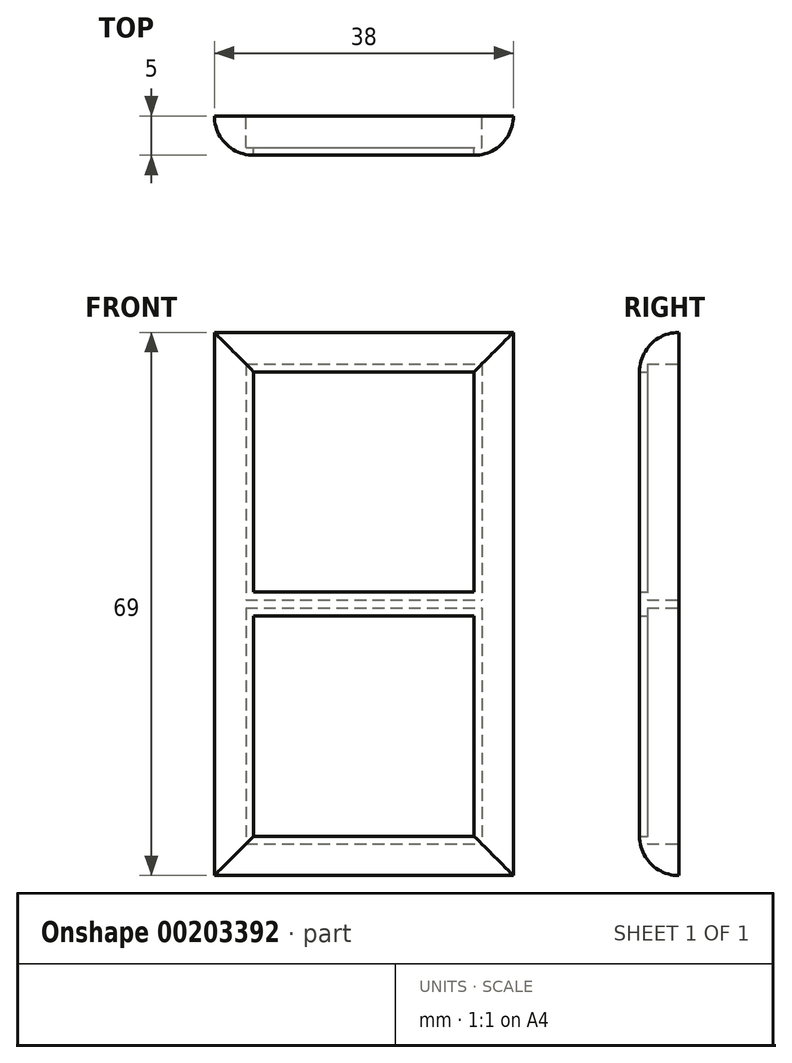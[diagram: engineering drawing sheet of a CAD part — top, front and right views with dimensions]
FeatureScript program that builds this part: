
annotation { "Feature Type Name" : "Feature", "Feature Type Description" : "" }
export const myFeature = defineFeature(function(context is Context, id is Id, definition is map)
    precondition{}
    {
        {
            var Q0;
            Q0=qCreatedBy(makeId("Front.planeOp"),FACE);
            var sketch = newSketch(context, id + "F0", { "sketchPlane" : qUnion([Q0])});
            skLineSegment(sketch, "E0.bottom", {"start": v(-19, 34.5) * mm, "end": v(19, 34.5) * mm});
            skLineSegment(sketch, "E0.top", {"start": v(-19, -34.5) * mm, "end": v(19, -34.5) * mm});
            skLineSegment(sketch, "E0.left", {"start": v(-19, 34.5) * mm, "end": v(-19, -34.5) * mm});
            skLineSegment(sketch, "E0.right", {"start": v(19, 34.5) * mm, "end": v(19, -34.5) * mm});
            skPoint(sketch, "E0.middle", {"position": v(0, 0) * mm});
            skLineSegment(sketch, "E1.bottom", {"start": v(-14, 29.5) * mm, "end": v(14, 29.5) * mm});
            skLineSegment(sketch, "E1.top", {"start": v(-14, -29.5) * mm, "end": v(14, -29.5) * mm});
            skLineSegment(sketch, "E1.left", {"start": v(-14, 29.5) * mm, "end": v(-14, -29.5) * mm});
            skLineSegment(sketch, "E1.right", {"start": v(14, 29.5) * mm, "end": v(14, -29.5) * mm});
            skLineSegment(sketch, "E2.bottom", {"start": v(-15, 30.5) * mm, "end": v(15, 30.5) * mm});
            skLineSegment(sketch, "E2.top", {"start": v(-15, -30.5) * mm, "end": v(15, -30.5) * mm});
            skLineSegment(sketch, "E2.left", {"start": v(-15, 30.5) * mm, "end": v(-15, -30.5) * mm});
            skLineSegment(sketch, "E2.right", {"start": v(15, 30.5) * mm, "end": v(15, -30.5) * mm});
            skLineSegment(sketch, "E3.bottom", {"start": v(-15, 0.5) * mm, "end": v(15, 0.5) * mm});
            skLineSegment(sketch, "E3.top", {"start": v(-15, -0.5) * mm, "end": v(15, -0.5) * mm});
            skLineSegment(sketch, "E3.left", {"start": v(-15, 0.5) * mm, "end": v(-15, -0.5) * mm});
            skLineSegment(sketch, "E3.right", {"start": v(15, 0.5) * mm, "end": v(15, -0.5) * mm});
            skLineSegment(sketch, "E4.bottom", {"start": v(-15, 1.5) * mm, "end": v(15, 1.5) * mm});
            skLineSegment(sketch, "E4.top", {"start": v(-15, -1.5) * mm, "end": v(15, -1.5) * mm});
            skLineSegment(sketch, "E4.left", {"start": v(-15, 1.5) * mm, "end": v(-15, -1.5) * mm});
            skLineSegment(sketch, "E4.right", {"start": v(15, 1.5) * mm, "end": v(15, -1.5) * mm});
            skSolve(sketch);
        }
        {
            var Q0;
            {var subQ7=sQuery(id+"F0.wireOp",EDGE,"E1.top");Q0=makeQuery(id+"F0.imprint","IMPRINT",FACE,{"disambiguationData":[TD([[makeQuery(id+"F0.imprint","IMPRINT",EDGE,{"derivedFrom":subQ7}),-1.0]])]});}
            var Q1;
            {var subQ2=sQuery(id+"F0.wireOp",EDGE,"E1.bottom");Q1=makeQuery(id+"F0.imprint","IMPRINT",FACE,{"disambiguationData":[TD([[makeQuery(id+"F0.imprint","IMPRINT",EDGE,{"derivedFrom":subQ2}),1.0]])]});}
            var Q2;
            {var subQ0=sQuery(id+"F0.wireOp",EDGE,"E1.bottom");Q2=makeQuery(id+"F0.imprint","IMPRINT",FACE,{"disambiguationData":[TD([[makeQuery(id+"F0.imprint","IMPRINT",EDGE,{"derivedFrom":subQ0}),-1.0]])]});}
            var Q3;
            Q3=makeQuery(id+"F0.imprint","IMPRINT",FACE,{"disambiguationData":[TD([[makeQuery(id+"F0.imprint","IMPRINT",EDGE,{"derivedFrom":sQuery(id+"F0.wireOp",EDGE,"E0.bottom")}),-1.0]])]});
            var Q4;
            {var subQ0=sQuery(id+"F0.wireOp",EDGE,"E1.top");Q4=makeQuery(id+"F0.imprint","IMPRINT",FACE,{"disambiguationData":[TD([[makeQuery(id+"F0.imprint","IMPRINT",EDGE,{"derivedFrom":subQ0}),1.0]])]});}
            var Q5;
            {var subQ0=sQuery(id+"F0.wireOp",EDGE,"E4.bottom");var subQ1=sQuery(id+"F0.wireOp",EDGE,"E1.left");var subQ2=makeQuery(id+"F0.imprint","INTERSECT",VERTEX,{"derivedFrom":[subQ1,subQ0]});Q5=makeQuery(id+"F0.imprint","IMPRINT",FACE,{"disambiguationData":[TD([[makeQuery(id+"F0.imprint","IMPRINT",EDGE,{"disambiguationData":[TD([[subQ2,-1.0]])],"derivedFrom":subQ1}),1.0]])]});}
            var Q6;
            {var subQ0=sQuery(id+"F0.wireOp",EDGE,"E3.top");var subQ1=sQuery(id+"F0.wireOp",EDGE,"E1.left");var subQ2=makeQuery(id+"F0.imprint","INTERSECT",VERTEX,{"derivedFrom":[subQ1,subQ0]});Q6=makeQuery(id+"F0.imprint","IMPRINT",FACE,{"disambiguationData":[TD([[makeQuery(id+"F0.imprint","IMPRINT",EDGE,{"disambiguationData":[TD([[subQ2,-1.0]])],"derivedFrom":subQ1}),1.0]])]});}
            var Q7;
            {var subQ0=sQuery(id+"F0.wireOp",EDGE,"E3.bottom");var subQ1=sQuery(id+"F0.wireOp",EDGE,"E1.left");var subQ2=makeQuery(id+"F0.imprint","INTERSECT",VERTEX,{"derivedFrom":[subQ1,subQ0]});Q7=makeQuery(id+"F0.imprint","IMPRINT",FACE,{"disambiguationData":[TD([[makeQuery(id+"F0.imprint","IMPRINT",EDGE,{"disambiguationData":[TD([[subQ2,-1.0]])],"derivedFrom":subQ1}),1.0]])]});}
            var Q8;
            {var subQ0=sQuery(id+"F0.wireOp",EDGE,"E4.bottom");var subQ1=sQuery(id+"F0.wireOp",EDGE,"E1.left");var subQ2=makeQuery(id+"F0.imprint","INTERSECT",VERTEX,{"derivedFrom":[subQ1,subQ0]});Q8=makeQuery(id+"F0.imprint","IMPRINT",FACE,{"disambiguationData":[TD([[makeQuery(id+"F0.imprint","IMPRINT",EDGE,{"disambiguationData":[TD([[subQ2,-1.0]])],"derivedFrom":subQ1}),-1.0]])]});}
            var Q9;
            {var subQ0=sQuery(id+"F0.wireOp",EDGE,"E3.bottom");var subQ1=sQuery(id+"F0.wireOp",EDGE,"E1.left");var subQ2=makeQuery(id+"F0.imprint","INTERSECT",VERTEX,{"derivedFrom":[subQ1,subQ0]});Q9=makeQuery(id+"F0.imprint","IMPRINT",FACE,{"disambiguationData":[TD([[makeQuery(id+"F0.imprint","IMPRINT",EDGE,{"disambiguationData":[TD([[subQ2,-1.0]])],"derivedFrom":subQ1}),-1.0]])]});}
            var Q10;
            {var subQ0=sQuery(id+"F0.wireOp",EDGE,"E3.top");var subQ1=sQuery(id+"F0.wireOp",EDGE,"E1.left");var subQ2=makeQuery(id+"F0.imprint","INTERSECT",VERTEX,{"derivedFrom":[subQ1,subQ0]});Q10=makeQuery(id+"F0.imprint","IMPRINT",FACE,{"disambiguationData":[TD([[makeQuery(id+"F0.imprint","IMPRINT",EDGE,{"disambiguationData":[TD([[subQ2,-1.0]])],"derivedFrom":subQ1}),-1.0]])]});}
            var Q11;
            {var subQ0=sQuery(id+"F0.wireOp",EDGE,"E4.bottom");var subQ1=sQuery(id+"F0.wireOp",EDGE,"E1.right");var subQ2=makeQuery(id+"F0.imprint","INTERSECT",VERTEX,{"derivedFrom":[subQ1,subQ0]});Q11=makeQuery(id+"F0.imprint","IMPRINT",FACE,{"disambiguationData":[TD([[makeQuery(id+"F0.imprint","IMPRINT",EDGE,{"disambiguationData":[TD([[subQ2,-1.0]])],"derivedFrom":subQ1}),1.0]])]});}
            var Q12;
            {var subQ0=sQuery(id+"F0.wireOp",EDGE,"E3.bottom");var subQ1=sQuery(id+"F0.wireOp",EDGE,"E1.right");var subQ2=makeQuery(id+"F0.imprint","INTERSECT",VERTEX,{"derivedFrom":[subQ1,subQ0]});Q12=makeQuery(id+"F0.imprint","IMPRINT",FACE,{"disambiguationData":[TD([[makeQuery(id+"F0.imprint","IMPRINT",EDGE,{"disambiguationData":[TD([[subQ2,-1.0]])],"derivedFrom":subQ1}),1.0]])]});}
            var Q13;
            {var subQ0=sQuery(id+"F0.wireOp",EDGE,"E3.top");var subQ1=sQuery(id+"F0.wireOp",EDGE,"E1.right");var subQ2=makeQuery(id+"F0.imprint","INTERSECT",VERTEX,{"derivedFrom":[subQ1,subQ0]});Q13=makeQuery(id+"F0.imprint","IMPRINT",FACE,{"disambiguationData":[TD([[makeQuery(id+"F0.imprint","IMPRINT",EDGE,{"disambiguationData":[TD([[subQ2,-1.0]])],"derivedFrom":subQ1}),1.0]])]});}
            extrude(context, id + "F1", {"entities" : qUnion([Q0, Q1, Q2, Q3, Q4, Q5, Q6, Q7, Q8, Q9, Q10, Q11, Q12, Q13]), "depth" : 5 * mm});
        }
        {
            var Q0;
            {var subQ0=sQuery(id+"F0.wireOp",EDGE,"E1.bottom");Q0=makeQuery(id+"F0.imprint","IMPRINT",FACE,{"disambiguationData":[TD([[makeQuery(id+"F0.imprint","IMPRINT",EDGE,{"derivedFrom":subQ0}),-1.0]])]});}
            var Q1;
            {var subQ0=sQuery(id+"F0.wireOp",EDGE,"E1.top");Q1=makeQuery(id+"F0.imprint","IMPRINT",FACE,{"disambiguationData":[TD([[makeQuery(id+"F0.imprint","IMPRINT",EDGE,{"derivedFrom":subQ0}),1.0]])]});}
            extrude(context, id + "F2", {"entities" : qUnion([Q0, Q1]), "operationType" : NewBodyOperationType.REMOVE, "depth" : 25 * mm});
        }
        {
            var Q0;
            {var subQ2=sQuery(id+"F0.wireOp",EDGE,"E1.bottom");Q0=makeQuery(id+"F0.imprint","IMPRINT",FACE,{"disambiguationData":[TD([[makeQuery(id+"F0.imprint","IMPRINT",EDGE,{"derivedFrom":subQ2}),1.0]])]});}
            var Q1;
            {var subQ0=sQuery(id+"F0.wireOp",EDGE,"E4.bottom");var subQ1=sQuery(id+"F0.wireOp",EDGE,"E1.right");var subQ2=makeQuery(id+"F0.imprint","INTERSECT",VERTEX,{"derivedFrom":[subQ1,subQ0]});Q1=makeQuery(id+"F0.imprint","IMPRINT",FACE,{"disambiguationData":[TD([[makeQuery(id+"F0.imprint","IMPRINT",EDGE,{"disambiguationData":[TD([[subQ2,-1.0]])],"derivedFrom":subQ1}),1.0]])]});}
            var Q2;
            {var subQ0=sQuery(id+"F0.wireOp",EDGE,"E4.bottom");var subQ1=sQuery(id+"F0.wireOp",EDGE,"E1.left");var subQ2=makeQuery(id+"F0.imprint","INTERSECT",VERTEX,{"derivedFrom":[subQ1,subQ0]});Q2=makeQuery(id+"F0.imprint","IMPRINT",FACE,{"disambiguationData":[TD([[makeQuery(id+"F0.imprint","IMPRINT",EDGE,{"disambiguationData":[TD([[subQ2,-1.0]])],"derivedFrom":subQ1}),1.0]])]});}
            var Q3;
            {var subQ0=sQuery(id+"F0.wireOp",EDGE,"E4.bottom");var subQ1=sQuery(id+"F0.wireOp",EDGE,"E1.left");var subQ2=makeQuery(id+"F0.imprint","INTERSECT",VERTEX,{"derivedFrom":[subQ1,subQ0]});Q3=makeQuery(id+"F0.imprint","IMPRINT",FACE,{"disambiguationData":[TD([[makeQuery(id+"F0.imprint","IMPRINT",EDGE,{"disambiguationData":[TD([[subQ2,-1.0]])],"derivedFrom":subQ1}),-1.0]])]});}
            var Q4;
            {var subQ7=sQuery(id+"F0.wireOp",EDGE,"E1.top");Q4=makeQuery(id+"F0.imprint","IMPRINT",FACE,{"disambiguationData":[TD([[makeQuery(id+"F0.imprint","IMPRINT",EDGE,{"derivedFrom":subQ7}),-1.0]])]});}
            var Q5;
            {var subQ0=sQuery(id+"F0.wireOp",EDGE,"E3.top");var subQ1=sQuery(id+"F0.wireOp",EDGE,"E1.right");var subQ2=makeQuery(id+"F0.imprint","INTERSECT",VERTEX,{"derivedFrom":[subQ1,subQ0]});Q5=makeQuery(id+"F0.imprint","IMPRINT",FACE,{"disambiguationData":[TD([[makeQuery(id+"F0.imprint","IMPRINT",EDGE,{"disambiguationData":[TD([[subQ2,-1.0]])],"derivedFrom":subQ1}),1.0]])]});}
            var Q6;
            {var subQ0=sQuery(id+"F0.wireOp",EDGE,"E3.top");var subQ1=sQuery(id+"F0.wireOp",EDGE,"E1.left");var subQ2=makeQuery(id+"F0.imprint","INTERSECT",VERTEX,{"derivedFrom":[subQ1,subQ0]});Q6=makeQuery(id+"F0.imprint","IMPRINT",FACE,{"disambiguationData":[TD([[makeQuery(id+"F0.imprint","IMPRINT",EDGE,{"disambiguationData":[TD([[subQ2,-1.0]])],"derivedFrom":subQ1}),1.0]])]});}
            var Q7;
            {var subQ0=sQuery(id+"F0.wireOp",EDGE,"E3.top");var subQ1=sQuery(id+"F0.wireOp",EDGE,"E1.left");var subQ2=makeQuery(id+"F0.imprint","INTERSECT",VERTEX,{"derivedFrom":[subQ1,subQ0]});Q7=makeQuery(id+"F0.imprint","IMPRINT",FACE,{"disambiguationData":[TD([[makeQuery(id+"F0.imprint","IMPRINT",EDGE,{"disambiguationData":[TD([[subQ2,-1.0]])],"derivedFrom":subQ1}),-1.0]])]});}
            extrude(context, id + "F3", {"entities" : qUnion([Q0, Q1, Q2, Q3, Q4, Q5, Q6, Q7]), "operationType" : NewBodyOperationType.REMOVE, "depth" : 4 * mm});
        }
        {
            var Q0;
            Q0=makeQuery(id+"F1.opExtrude","CAP_EDGE",EDGE,{"disambiguationData":[OSD([sQuery(id+"F0.wireOp",EDGE,"E0.left")])],"isStart":false});
            var Q1;
            Q1=makeQuery(id+"F1.opExtrude","CAP_EDGE",EDGE,{"disambiguationData":[OSD([sQuery(id+"F0.wireOp",EDGE,"E0.bottom")])],"isStart":false});
            var Q2;
            Q2=makeQuery(id+"F1.opExtrude","CAP_EDGE",EDGE,{"disambiguationData":[OSD([sQuery(id+"F0.wireOp",EDGE,"E0.right")])],"isStart":false});
            var Q3;
            Q3=makeQuery(id+"F1.opExtrude","CAP_EDGE",EDGE,{"disambiguationData":[OSD([sQuery(id+"F0.wireOp",EDGE,"E0.top")])],"isStart":false});
            fillet(context, id + "F4", {"entities" : qUnion([Q0, Q1, Q2, Q3]), "radius" : 5 * mm, "tangentPropagation" : true, "allowEdgeOverflow" : false});
        }
    });
